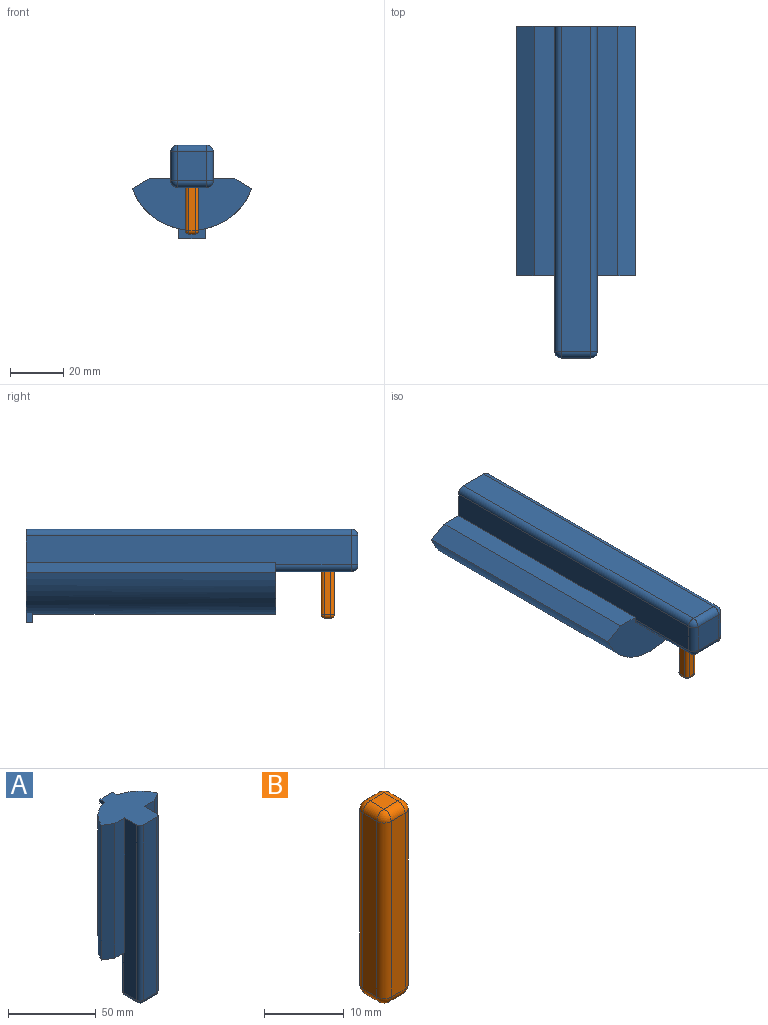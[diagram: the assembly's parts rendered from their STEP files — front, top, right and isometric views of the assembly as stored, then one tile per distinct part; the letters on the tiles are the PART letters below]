
ASSEMBLY  parts=2 mates=1
PART A: 33 faces, bbox 45x35.3x125 mm
  f0: plane 44.99x19.5mm, normal (0,0,-1), area 606.3mm2, adj f2,f3,f4,f6,f7,f24,f25,f26
  f1: plane 44.99x35.27mm, normal (0,0,1), area 891.8mm2, adj f5,f6,f7,f17,f23,f24,f25,f26
  f2: plane 28.45x10.92mm, normal (0,1,0), area 285.7mm2, adj f0,f3,f4,f9,f10,f11,f12,f15
  f3: cylinder r=2.54mm len=28.45mm, axis (0,0,-1), area 113.5mm2, adj f0,f2,f7,f14
  f4: cylinder r=2.54mm len=28.45mm, axis (0,0,1), area 113.5mm2, adj f0,f2,f6,f18
  f5: plane 122.43x10.92mm, normal (0,-1,0), area 1336.9mm2, adj f1,f17,f21,f23
  f6: plane 122.43x10.92mm, normal (1,0,0), area 1246.7mm2, adj f0,f1,f4,f20,f23,f31
  f7: plane 122.43x10.92mm, normal (-1,0,0), area 1246.7mm2, adj f0,f1,f3,f16,f17,f32
  f8: plane 10.92x10.92mm, normal (0,0,-1), area 119.2mm2, adj f15,f16,f20,f21
  f9: plane 12x5mm, normal (0,0,1), area 60mm2, adj f2,f10,f12,f13
  f10: plane 12x5mm, normal (1,0,0), area 60mm2, adj f2,f9,f11,f13
  f11: plane 12x5mm, normal (0,0,-1), area 60mm2, adj f2,f10,f12,f13
  f12: plane 12x5mm, normal (-1,0,0), area 60mm2, adj f2,f9,f11,f13
  f13: plane 5x5mm, normal (0,1,0), area 25mm2, adj f9,f10,f11,f12
  f14: sphere r=2.54mm, area 10.1mm2, adj f3,f15,f16
  f15: cylinder r=2.54mm len=10.92mm, axis (1,0,0), area 43.6mm2, adj f2,f8,f14,f18
  f16: cylinder r=2.54mm len=10.92mm, axis (0,1,0), area 43.6mm2, adj f7,f8,f14,f19
  f17: cylinder r=2.54mm len=122.43mm, axis (0,0,1), area 488.5mm2, adj f1,f5,f7,f19
  f18: sphere r=2.54mm, area 10.1mm2, adj f4,f15,f20
  f19: sphere r=2.54mm, area 10.1mm2, adj f16,f17,f21
  f20: cylinder r=2.54mm len=10.92mm, axis (0,-1,0), area 43.6mm2, adj f6,f8,f18,f22
  f21: cylinder r=2.54mm len=10.92mm, axis (-1,0,0), area 43.6mm2, adj f5,f8,f19,f22
  f22: sphere r=2.54mm, area 10.1mm2, adj f20,f21,f23
  f23: cylinder r=2.54mm len=122.43mm, axis (0,0,-1), area 488.5mm2, adj f1,f5,f6,f22
  f24: plane 93.98x6.7mm, normal (-0.5,-0.87,0), area 727mm2, adj f0,f1,f26,f32
  f25: plane 93.98x6.7mm, normal (0.5,-0.87,0), area 727mm2, adj f0,f1,f26,f31
  f26: cylinder r=24mm len=93.98mm, axis (0,0,1), area 5453.3mm2, adj f0,f1,f24,f25,f27,f29,f30
  f27: plane 3.81x2.54mm, normal (1,0,0), area 9.7mm2, adj f1,f26,f28,f30
  f28: plane 10.16x2.54mm, normal (0,1,0), area 25.8mm2, adj f1,f27,f29,f30
  f29: plane 3.81x2.54mm, normal (-1,0,0), area 9.7mm2, adj f1,f26,f28,f30
  f30: plane 10.16x3.81mm, normal (0,0,-1), area 35mm2, adj f26,f27,f28,f29
  f31: plane 93.98x7.79mm, normal (0,-1,0), area 732.5mm2, adj f0,f1,f6,f25
  f32: plane 93.98x7.79mm, normal (0,-1,0), area 732.5mm2, adj f0,f1,f7,f24
PART B: 26 faces, bbox 5x5x29.5 mm
  f0: plane 26.92x2.46mm, normal (0,-1,0), area 66.2mm2, adj f14,f19,f22,f25
  f1: plane 26.92x2.46mm, normal (1,0,0), area 66.2mm2, adj f11,f20,f21,f25
  f2: plane 26.92x2.46mm, normal (0,1,0), area 66.2mm2, adj f6,f10,f11,f12
  f3: plane 26.92x2.46mm, normal (-1,0,0), area 66.2mm2, adj f6,f9,f13,f14
  f4: plane 2.46x2.46mm, normal (0,0,1), area 6.1mm2, adj f9,f10,f19,f20
  f5: plane 2.46x2.46mm, normal (0,0,-1), area 6.1mm2, adj f12,f13,f21,f22
  f6: cylinder r=1.27mm len=26.92mm, axis (0,0,1), area 53.7mm2, adj f2,f3,f7,f8
  f7: sphere r=1.27mm, area 2.5mm2, adj f6,f9,f10
  f8: sphere r=1.27mm, area 2.5mm2, adj f6,f12,f13
  f9: cylinder r=1.27mm len=2.46mm, axis (0,1,0), area 4.9mm2, adj f3,f4,f7,f15
  f10: cylinder r=1.27mm len=2.46mm, axis (1,0,0), area 4.9mm2, adj f2,f4,f7,f16
  f11: cylinder r=1.27mm len=26.92mm, axis (0,0,-1), area 53.7mm2, adj f1,f2,f16,f17
  f12: cylinder r=1.27mm len=2.46mm, axis (-1,0,0), area 4.9mm2, adj f2,f5,f8,f17
  f13: cylinder r=1.27mm len=2.46mm, axis (0,-1,0), area 4.9mm2, adj f3,f5,f8,f18
  f14: cylinder r=1.27mm len=26.92mm, axis (0,0,-1), area 53.7mm2, adj f0,f3,f15,f18
  f15: sphere r=1.27mm, area 2.5mm2, adj f9,f14,f19
  f16: sphere r=1.27mm, area 2.5mm2, adj f10,f11,f20
  f17: sphere r=1.27mm, area 2.5mm2, adj f11,f12,f21
  f18: sphere r=1.27mm, area 2.5mm2, adj f13,f14,f22
  f19: cylinder r=1.27mm len=2.46mm, axis (-1,0,0), area 4.9mm2, adj f0,f4,f15,f23
  f20: cylinder r=1.27mm len=2.46mm, axis (0,-1,0), area 4.9mm2, adj f1,f4,f16,f23
  f21: cylinder r=1.27mm len=2.46mm, axis (0,1,0), area 4.9mm2, adj f1,f5,f17,f24
  f22: cylinder r=1.27mm len=2.46mm, axis (1,0,0), area 4.9mm2, adj f0,f5,f18,f24
  f23: sphere r=1.27mm, area 2.5mm2, adj f19,f20,f25
  f24: sphere r=1.27mm, area 2.5mm2, adj f21,f22,f25
  f25: cylinder r=1.27mm len=26.92mm, axis (0,0,1), area 53.7mm2, adj f0,f1,f23,f24
PLACE A rot(axis=(-1,0,0),90deg) t=(-8.22,107.74,-8.47)mm
PLACE B t=(-8.22,-5.83,-33.94)mm
MATE fastened B.f4 <-> A.f13  axis (0,0,1) through (-8.22,-5.83,-4.47)mm
